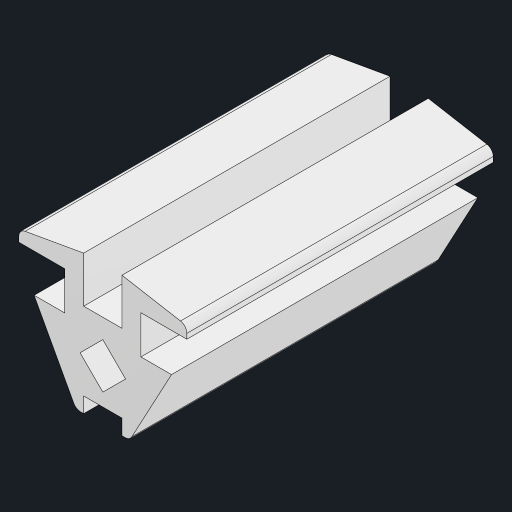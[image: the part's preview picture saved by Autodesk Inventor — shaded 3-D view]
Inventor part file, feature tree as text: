
AUTODESK INVENTOR PART (.ipt)
format: ipt  version: 2023 (Build 270158000, 158)  size: 166,400 bytes
history: native  units: mm
features: other x1, extrude x1, fillet x1, sketch x1
ambient origin geometry x8: Origin, YZ Plane, XZ Plane, XY Plane, X Axis, Y Axis, Z Axis, Center Point
bodies: Body1 (feature_tree)
feature tree (4):
  other  "ソリッド1"
  extrude  "押し出し1"  Depth=40.0mm TaperAngle=0.0deg
  fillet  "フィレット2"  Radius=2.0mm
  sketch  "スケッチ1"
